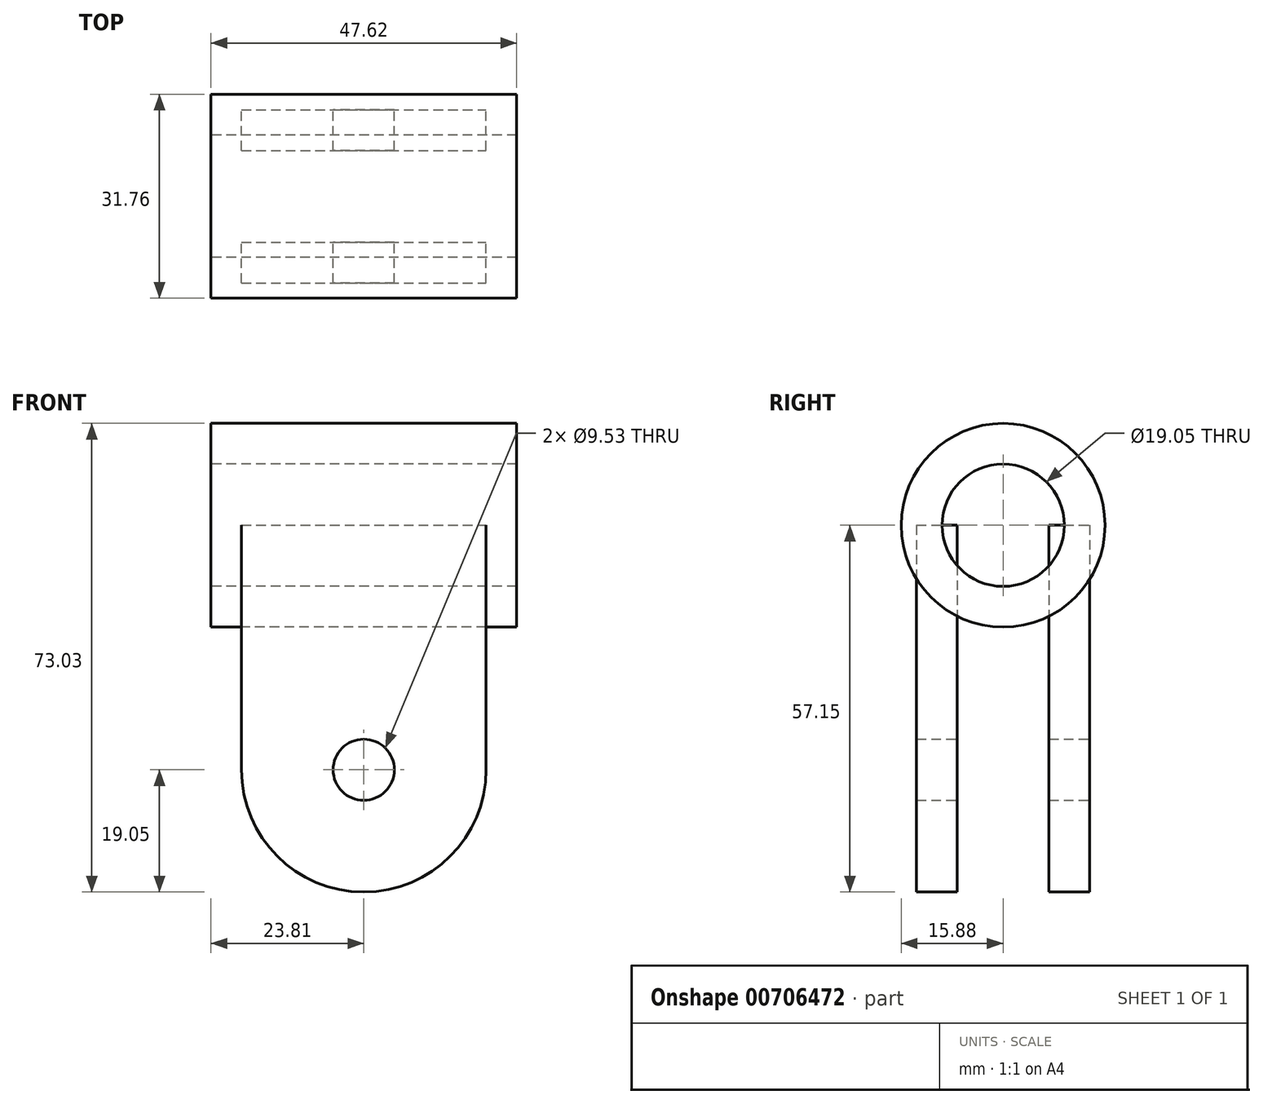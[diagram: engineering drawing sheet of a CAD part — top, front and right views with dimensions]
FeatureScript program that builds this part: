
annotation { "Feature Type Name" : "Feature", "Feature Type Description" : "" }
export const myFeature = defineFeature(function(context is Context, id is Id, definition is map)
    precondition{}
    {
        {
            var Q0;
            Q0=qCreatedBy(makeId("Front.planeOp"),FACE);
            var sketch = newSketch(context, id + "F0", { "sketchPlane" : qUnion([Q0])});
            skCircle(sketch, "E0", {"center": v(0, 0) * mm, "radius": 19.05 * mm});
            skCircle(sketch, "E1", {"center": v(0, 0) * mm, "radius": 4.76 * mm});
            skLineSegment(sketch, "E2.bottom", {"start": v(-19.05, 38.1) * mm, "end": v(19.05, 38.1) * mm});
            skLineSegment(sketch, "E2.top", {"start": v(-19.05, 0) * mm, "end": v(19.05, 0) * mm});
            skLineSegment(sketch, "E2.left", {"start": v(-19.05, 38.1) * mm, "end": v(-19.05, 0) * mm});
            skLineSegment(sketch, "E2.right", {"start": v(19.05, 38.1) * mm, "end": v(19.05, 0) * mm});
            skPoint(sketch, "E3", {"position": v(0, 38.1) * mm});
            skLineSegment(sketch, "E4.bottom", {"start": v(-23.81, 41.27) * mm, "end": v(23.81, 41.27) * mm});
            skLineSegment(sketch, "E4.top", {"start": v(-23.81, 34.92) * mm, "end": v(23.81, 34.92) * mm});
            skLineSegment(sketch, "E4.left", {"start": v(-23.81, 41.28) * mm, "end": v(-23.81, 34.92) * mm});
            skLineSegment(sketch, "E4.right", {"start": v(23.81, 41.28) * mm, "end": v(23.81, 34.92) * mm});
            skPoint(sketch, "E5", {"position": v(0, 41.27) * mm});
            skPoint(sketch, "E6", {"position": v(-23.81, 38.1) * mm});
            skLineSegment(sketch, "E7", {"start": v(-23.8, 50.8) * mm, "end": v(23.82, 50.8) * mm});
            skSolve(sketch);
        }
        {
            var Q0;
            {var subQ0=sQuery(id+"F0.wireOp",EDGE,"E2.top");var subQ4=sQuery(id+"F0.wireOp",EDGE,"E1");var subQ5=makeQuery(id+"F0.imprint","INTERSECT",VERTEX,{"disambiguationData":[OD(0.0)],"derivedFrom":[subQ4,subQ0]});Q0=makeQuery(id+"F0.imprint","IMPRINT",FACE,{"disambiguationData":[TD([[makeQuery(id+"F0.imprint","IMPRINT",EDGE,{"disambiguationData":[TD([[subQ5,1.0]])],"derivedFrom":subQ4}),-1.0]])]});}
            var Q1;
            {var subQ0=sQuery(id+"F0.wireOp",EDGE,"E2.top");var subQ4=sQuery(id+"F0.wireOp",EDGE,"E1");var subQ5=makeQuery(id+"F0.imprint","INTERSECT",VERTEX,{"disambiguationData":[OD(0.0)],"derivedFrom":[subQ4,subQ0]});Q1=makeQuery(id+"F0.imprint","IMPRINT",FACE,{"disambiguationData":[TD([[makeQuery(id+"F0.imprint","IMPRINT",EDGE,{"disambiguationData":[TD([[subQ5,-1.0]])],"derivedFrom":subQ4}),-1.0]])]});}
            var Q2;
            {var subQ0=sQuery(id+"F0.wireOp",EDGE,"E2.left");var subQ6=sQuery(id+"F0.wireOp",EDGE,"E4.top");var subQ7=makeQuery(id+"F0.imprint","INTERSECT",VERTEX,{"derivedFrom":[subQ0,subQ6]});Q2=makeQuery(id+"F0.imprint","IMPRINT",FACE,{"disambiguationData":[TD([[makeQuery(id+"F0.imprint","IMPRINT",EDGE,{"disambiguationData":[TD([[subQ7,-1.0]])],"derivedFrom":subQ6}),-1.0]])]});}
            var Q3;
            {var subQ0=sQuery(id+"F0.wireOp",EDGE,"E2.bottom");Q3=makeQuery(id+"F0.imprint","IMPRINT",FACE,{"disambiguationData":[TD([[makeQuery(id+"F0.imprint","IMPRINT",EDGE,{"derivedFrom":subQ0}),-1.0]])]});}
            extrude(context, id + "F1", {"entities" : qUnion([Q0, Q1, Q2, Q3]), "depth" : 13.5 * mm, "offsetDistance" : 25.4 * mm, "hasSecondDirection" : true, "secondDirectionOppositeDirection" : true, "secondDirectionDepth" : -7.14 * mm});
        }
        {
            var Q0;
            Q0=makeQuery(id+"F1.opExtrude","SWEPT_BODY",BODY,{"disambiguationData":[OSD([sQuery(id+"F0.wireOp",EDGE,"E0"),sQuery(id+"F0.wireOp",EDGE,"E1"),sQuery(id+"F0.wireOp",EDGE,"E2.bottom"),sQuery(id+"F0.wireOp",EDGE,"E2.left"),sQuery(id+"F0.wireOp",EDGE,"E2.right")])]});
            transform(context, id + "F2", {"entities" : qUnion([Q0]), "transformType" : TransformType.TRANSLATION_3D, "dx" : 0 * mm, "dy" : 20.64 * mm, "dz" : 0 * mm, "makeCopy" : true});
        }
        {
            var Q0;
            {var subQ1=sQuery(id+"F0.wireOp",EDGE,"E2.bottom");Q0=makeQuery(id+"F0.imprint","IMPRINT",FACE,{"disambiguationData":[TD([[makeQuery(id+"F0.imprint","IMPRINT",EDGE,{"derivedFrom":subQ1}),1.0]])]});}
            var Q1;
            {var subQ0=sQuery(id+"F0.wireOp",EDGE,"E2.bottom");Q1=makeQuery(id+"F0.imprint","IMPRINT",FACE,{"disambiguationData":[TD([[makeQuery(id+"F0.imprint","IMPRINT",EDGE,{"derivedFrom":subQ0}),-1.0]])]});}
            var Q2;
            Q2=sQuery(id+"F0.wireOp",EDGE,"E7");
            revolve(context, id + "F3", {"surfaceOperationType" : NewSurfaceOperationType.NEW, "entities" : qUnion([Q0, Q1]), "axis" : qUnion([Q2]), "revolveType" : RevolveType.FULL});
        }
        {
            var Q0;
            Q0=makeQuery(id+"F3.opRevolve","SWEPT_BODY",BODY,{"disambiguationData":[OSD([sQuery(id+"F0.wireOp",EDGE,"E4.bottom"),sQuery(id+"F0.wireOp",EDGE,"E4.top"),sQuery(id+"F0.wireOp",EDGE,"E4.left"),sQuery(id+"F0.wireOp",EDGE,"E4.right")])]});
            transform(context, id + "F4", {"entities" : qUnion([Q0]), "transformType" : TransformType.TRANSLATION_3D, "dx" : 0 * mm, "dy" : 0 * mm, "dz" : -12.7 * mm, "makeCopy" : false});
        }
    });
